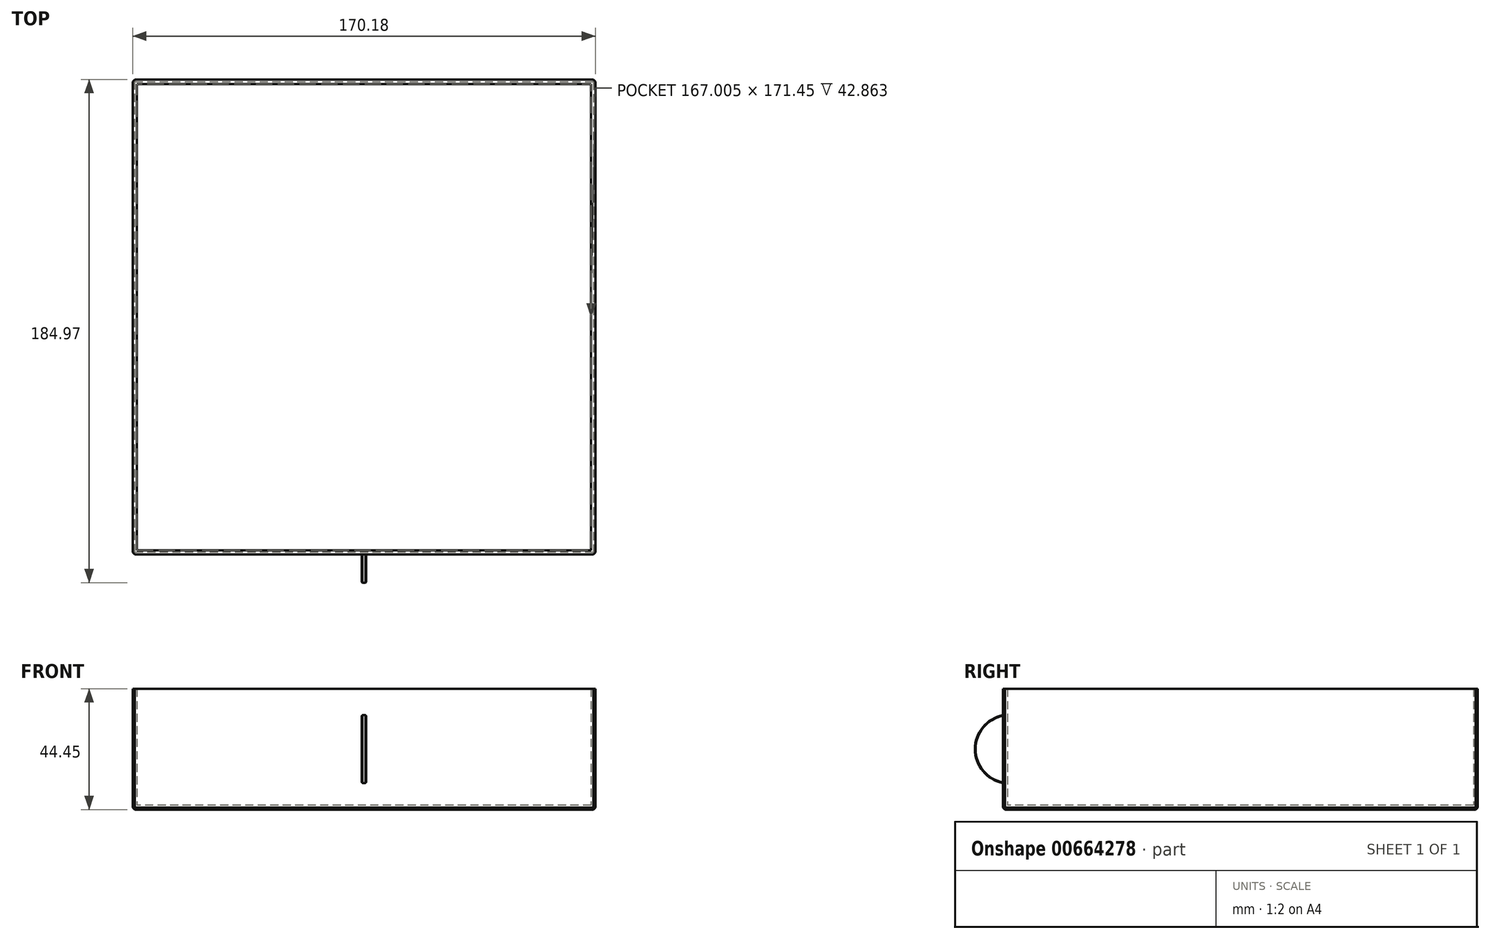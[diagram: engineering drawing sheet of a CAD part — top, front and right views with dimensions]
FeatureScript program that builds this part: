
annotation { "Feature Type Name" : "Feature", "Feature Type Description" : "" }
export const myFeature = defineFeature(function(context is Context, id is Id, definition is map)
    precondition{}
    {
        {
            var Q0;
            Q0=qCreatedBy(makeId("Top.planeOp"),FACE);
            var sketch = newSketch(context, id + "F0", { "sketchPlane" : qUnion([Q0])});
            skLineSegment(sketch, "E0.bottom", {"start": v(-85.1, 87.31) * mm, "end": v(85.1, 87.31) * mm});
            skLineSegment(sketch, "E0.top", {"start": v(-85.1, -87.31) * mm, "end": v(85.1, -87.31) * mm});
            skLineSegment(sketch, "E0.left", {"start": v(-85.1, 87.31) * mm, "end": v(-85.1, -87.31) * mm});
            skLineSegment(sketch, "E0.right", {"start": v(85.1, 87.31) * mm, "end": v(85.1, -87.31) * mm});
            skSolve(sketch);
        }
        {
            var Q0;
            Q0=qSketchRegion(id+"F0",true);
            extrude(context, id + "F1", {"entities" : qUnion([Q0]), "depth" : 1.59 * mm, "offsetDistance" : 25.4 * mm});
        }
        {
            var Q0;
            Q0=makeQuery(id+"F1.opExtrude","CAP_FACE",FACE,{"disambiguationData":[OSD([sQuery(id+"F0.wireOp",EDGE,"E0.bottom"),sQuery(id+"F0.wireOp",EDGE,"E0.top"),sQuery(id+"F0.wireOp",EDGE,"E0.left"),sQuery(id+"F0.wireOp",EDGE,"E0.right")])],"isStart":false});
            var sketch = newSketch(context, id + "F2", { "sketchPlane" : qUnion([Q0])});
            skLineSegment(sketch, "E1.0", {"start": v(-83.5, 85.73) * mm, "end": v(-83.5, -85.73) * mm});
            skLineSegment(sketch, "E1.1", {"start": v(83.5, 85.73) * mm, "end": v(-83.5, 85.73) * mm});
            skLineSegment(sketch, "E1.2", {"start": v(83.5, -85.73) * mm, "end": v(83.5, 85.73) * mm});
            skLineSegment(sketch, "E1.3", {"start": v(-83.5, -85.73) * mm, "end": v(83.5, -85.73) * mm});
            skLineSegment(sketch, "E2.0", {"start": v(-85.1, 87.31) * mm, "end": v(-85.1, -87.31) * mm});
            skLineSegment(sketch, "E2.1", {"start": v(-85.1, -87.31) * mm, "end": v(85.1, -87.31) * mm});
            skLineSegment(sketch, "E2.2", {"start": v(85.1, 87.31) * mm, "end": v(85.1, -87.31) * mm});
            skLineSegment(sketch, "E2.3", {"start": v(-85.1, 87.31) * mm, "end": v(85.1, 87.31) * mm});
            skSolve(sketch);
        }
        {
            var Q0;
            Q0=qSketchRegion(id+"F2",true);
            extrude(context, id + "F3", {"entities" : qUnion([Q0]), "operationType" : NewBodyOperationType.ADD, "depth" : 42.86 * mm, "offsetDistance" : 25.4 * mm});
        }
        {
            var Q0;
            Q0=qCreatedBy(makeId("Right.planeOp"),FACE);
            var sketch = newSketch(context, id + "F4", { "sketchPlane" : qUnion([Q0])});
            skArc(sketch, "E3", {"start": v(-87.31, 34.7) * mm, "mid": v(-97.66, 22.23) * mm, "end": v(-87.31, 9.74) * mm});
            skLineSegment(sketch, "E4", {"start": v(-87.31, 34.7) * mm, "end": v(-87.31, 9.74) * mm});
            skSolve(sketch);
        }
        {
            var Q0;
            Q0=qSketchRegion(id+"F4",true);
            extrude(context, id + "F5", {"entities" : qUnion([Q0]), "operationType" : NewBodyOperationType.ADD, "endBound" : BoundingType.SYMMETRIC, "depth" : 1.59 * mm, "offsetDistance" : 25.4 * mm});
        }
        {
            var Q0;
            Q0=makeQuery(id+"F1.opExtrude","CAP_EDGE",EDGE,{"disambiguationData":[OSD([sQuery(id+"F0.wireOp",EDGE,"E0.top")])],"isStart":true});
            var Q1;
            Q1=makeQuery(id+"F1.opExtrude","CAP_EDGE",EDGE,{"disambiguationData":[OSD([sQuery(id+"F0.wireOp",EDGE,"E0.left")])],"isStart":true});
            var Q2;
            Q2=makeQuery(id+"F1.opExtrude","CAP_EDGE",EDGE,{"disambiguationData":[OSD([sQuery(id+"F0.wireOp",EDGE,"E0.right")])],"isStart":true});
            var Q3;
            Q3=makeQuery(id+"F1.opExtrude","CAP_EDGE",EDGE,{"disambiguationData":[OSD([sQuery(id+"F0.wireOp",EDGE,"E0.bottom")])],"isStart":true});
            var Q4;
            Q4=makeQuery(id+"F3.boolean.opBoolean","MERGE",EDGE,{"derivedFrom":[makeQuery(id+"F1.opExtrude","SWEPT_EDGE",EDGE,{"disambiguationData":[OSD([sQuery(id+"F0.wireOp",EDGE,"E0.top"),sQuery(id+"F0.wireOp",EDGE,"E0.right")])]}),makeQuery(id+"F3.opExtrude","SWEPT_EDGE",EDGE,{"disambiguationData":[OSD([sQuery(id+"F2.wireOp",EDGE,"E2.1"),sQuery(id+"F2.wireOp",EDGE,"E2.2")])]})]});
            var Q5;
            Q5=makeQuery(id+"F3.boolean.opBoolean","MERGE",EDGE,{"derivedFrom":[makeQuery(id+"F1.opExtrude","SWEPT_EDGE",EDGE,{"disambiguationData":[OSD([sQuery(id+"F0.wireOp",EDGE,"E0.top"),sQuery(id+"F0.wireOp",EDGE,"E0.left")])]}),makeQuery(id+"F3.opExtrude","SWEPT_EDGE",EDGE,{"disambiguationData":[OSD([sQuery(id+"F2.wireOp",EDGE,"E2.0"),sQuery(id+"F2.wireOp",EDGE,"E2.1")])]})]});
            var Q6;
            Q6=makeQuery(id+"F3.boolean.opBoolean","MERGE",EDGE,{"derivedFrom":[makeQuery(id+"F1.opExtrude","SWEPT_EDGE",EDGE,{"disambiguationData":[OSD([sQuery(id+"F0.wireOp",EDGE,"E0.bottom"),sQuery(id+"F0.wireOp",EDGE,"E0.right")])]}),makeQuery(id+"F3.opExtrude","SWEPT_EDGE",EDGE,{"disambiguationData":[OSD([sQuery(id+"F2.wireOp",EDGE,"E2.2"),sQuery(id+"F2.wireOp",EDGE,"E2.3")])]})]});
            var Q7;
            Q7=makeQuery(id+"F3.boolean.opBoolean","MERGE",EDGE,{"derivedFrom":[makeQuery(id+"F1.opExtrude","SWEPT_EDGE",EDGE,{"disambiguationData":[OSD([sQuery(id+"F0.wireOp",EDGE,"E0.bottom"),sQuery(id+"F0.wireOp",EDGE,"E0.left")])]}),makeQuery(id+"F3.opExtrude","SWEPT_EDGE",EDGE,{"disambiguationData":[OSD([sQuery(id+"F2.wireOp",EDGE,"E2.0"),sQuery(id+"F2.wireOp",EDGE,"E2.3")])]})]});
            chamfer(context, id + "F6", {"entities" : qUnion([Q0, Q1, Q2, Q3, Q4, Q5, Q6, Q7]), "width" : 0.76 * mm, "tangentPropagation" : true});
        }
        {
            var Q0;
            Q0=makeQuery(id+"F5.opExtrude","CAP_EDGE",EDGE,{"disambiguationData":[OSD([sQuery(id+"F4.wireOp",EDGE,"E4")])],"isStart":false});
            var Q1;
            Q1=makeQuery(id+"F5.opExtrude","CAP_EDGE",EDGE,{"disambiguationData":[OSD([sQuery(id+"F4.wireOp",EDGE,"E3")])],"isStart":false});
            var Q2;
            Q2=makeQuery(id+"F5.opExtrude","CAP_EDGE",EDGE,{"disambiguationData":[OSD([sQuery(id+"F4.wireOp",EDGE,"E3")])],"isStart":true});
            var Q3;
            Q3=makeQuery(id+"F5.opExtrude","CAP_EDGE",EDGE,{"disambiguationData":[OSD([sQuery(id+"F4.wireOp",EDGE,"E4")])],"isStart":true});
            var Q4;
            {var subQ0=sQuery(id+"F4.wireOp",EDGE,"E4");var subQ1=sQuery(id+"F4.wireOp",EDGE,"E3");Q4=makeQuery(id+"F5.opExtrude","SWEPT_EDGE",EDGE,{"disambiguationData":[OSD([subQ1,subQ0]),TDD([makeQuery(id+"F4.imprint","INTERSECT",VERTEX,{"disambiguationData":[OD(0.0)],"derivedFrom":[subQ1,subQ0]})])]});}
            var Q5;
            {var subQ0=sQuery(id+"F4.wireOp",EDGE,"E4");var subQ1=sQuery(id+"F4.wireOp",EDGE,"E3");Q5=makeQuery(id+"F5.opExtrude","SWEPT_EDGE",EDGE,{"disambiguationData":[OSD([subQ1,subQ0]),TDD([makeQuery(id+"F4.imprint","INTERSECT",VERTEX,{"disambiguationData":[OD(1.0)],"derivedFrom":[subQ1,subQ0]})])]});}
            chamfer(context, id + "F7", {"entities" : qUnion([Q0, Q1, Q2, Q3, Q4, Q5]), "width" : 0.25 * mm, "tangentPropagation" : true});
        }
    });
